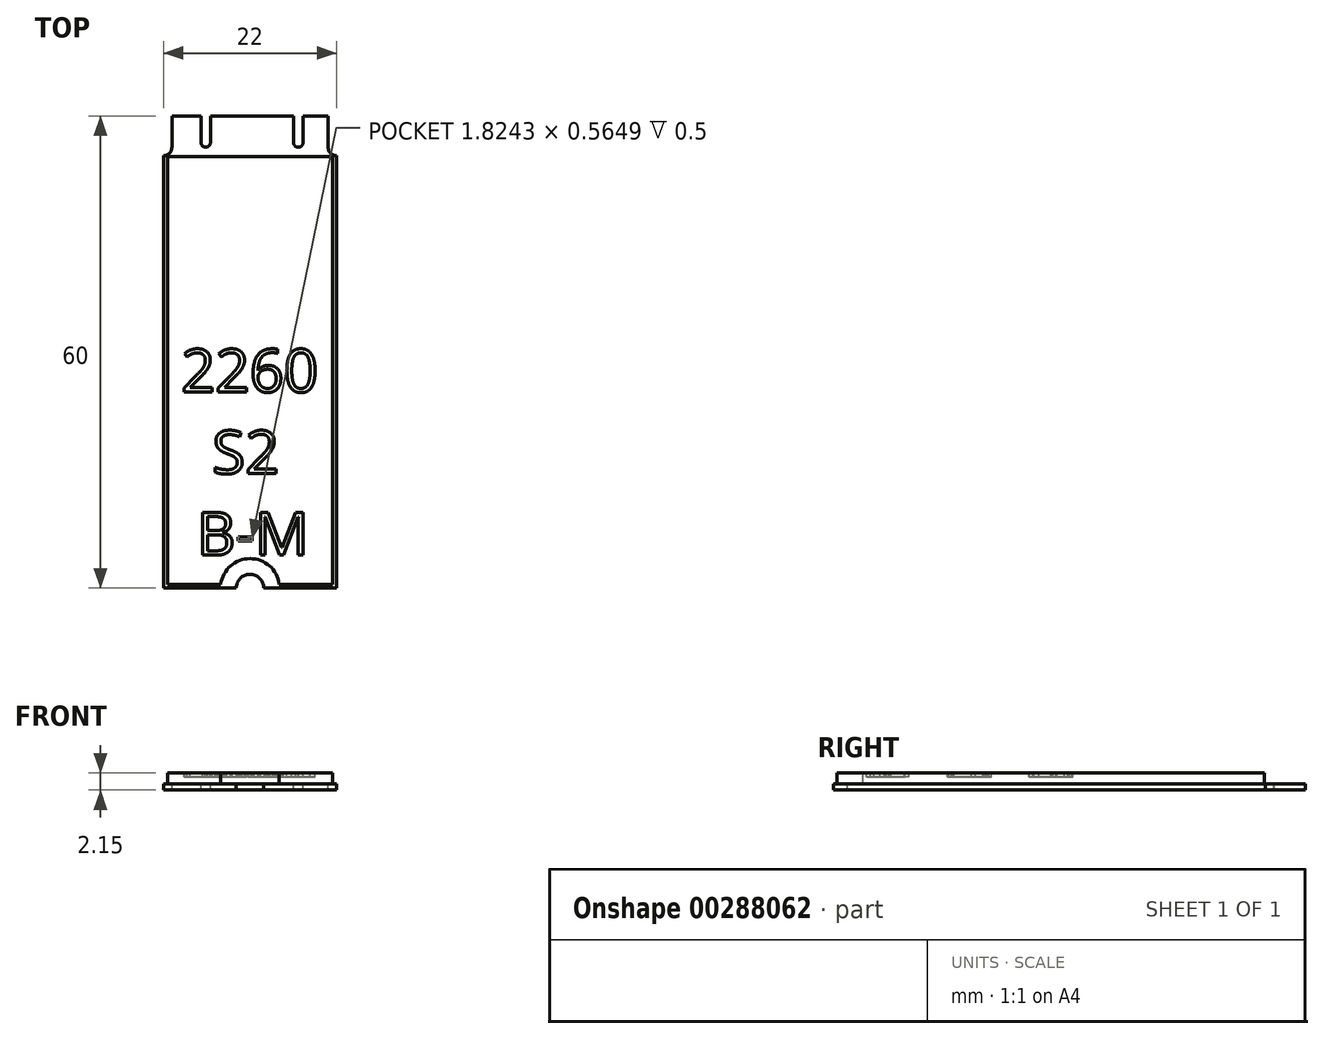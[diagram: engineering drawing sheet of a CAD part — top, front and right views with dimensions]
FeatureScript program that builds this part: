
annotation { "Feature Type Name" : "Feature", "Feature Type Description" : "" }
export const myFeature = defineFeature(function(context is Context, id is Id, definition is map)
    precondition{}
    {
        {
            assignVariable(context, id + "F0", {"name" : "thick", "anyValue" : .8});
        }
        {
            assignVariable(context, id + "F1", {"name" : "compheight", "anyValue" : 1.35});
        }
        {
            var Q0;
            Q0=qCreatedBy(makeId("Top.planeOp"),FACE);
            var sketch = newSketch(context, id + "F2", { "sketchPlane" : qUnion([Q0])});
            skLineSegment(sketch, "E0.bottom", {"start": v(-11, 30) * mm, "end": v(11, 30) * mm});
            skLineSegment(sketch, "E0.top", {"start": v(-11, -30) * mm, "end": v(11, -30) * mm});
            skLineSegment(sketch, "E0.left", {"start": v(-11, 30) * mm, "end": v(-11, -30) * mm});
            skLineSegment(sketch, "E0.right", {"start": v(11, 30) * mm, "end": v(11, -30) * mm});
            skPoint(sketch, "E0.middle", {"position": v(0, 0) * mm});
            skSolve(sketch);
        }
        {
            var Q0;
            Q0=qSketchRegion(id+"F2",true);
            extrude(context, id + "F3", {"entities" : qUnion([Q0]), "depth" : (getVariable(context, 'thick')) * mm});
        }
        {
            var Q0;
            Q0=makeQuery(id+"F3.opExtrude","CAP_FACE",FACE,{"disambiguationData":[OSD([sQuery(id+"F2.wireOp",EDGE,"E0.bottom"),sQuery(id+"F2.wireOp",EDGE,"E0.top"),sQuery(id+"F2.wireOp",EDGE,"E0.left"),sQuery(id+"F2.wireOp",EDGE,"E0.right")])],"isStart":false});
            var sketch = newSketch(context, id + "F4", { "sketchPlane" : qUnion([Q0])});
            skLineSegment(sketch, "E1.bottom", {"start": v(-10.5, -29.5) * mm, "end": v(10.5, -29.5) * mm});
            skLineSegment(sketch, "E1.top", {"start": v(-10.5, 24.8) * mm, "end": v(10.5, 24.8) * mm});
            skLineSegment(sketch, "E1.left", {"start": v(-10.5, -29.5) * mm, "end": v(-10.5, 24.8) * mm});
            skLineSegment(sketch, "E1.right", {"start": v(10.5, -29.5) * mm, "end": v(10.5, 24.8) * mm});
            skLineSegment(sketch, "E2", {"start": v(0, -30) * mm, "end": v(0, -29.5) * mm, "construction": true});
            skLineSegment(sketch, "E3", {"start": v(10.5, -2.35) * mm, "end": v(11, -2.35) * mm, "construction": true});
            skLineSegment(sketch, "E4", {"start": v(0, 24.8) * mm, "end": v(0, 30) * mm, "construction": true});
            skSolve(sketch);
        }
        {
            var Q0;
            Q0=qSketchRegion(id+"F4",true);
            extrude(context, id + "F5", {"entities" : qUnion([Q0]), "operationType" : NewBodyOperationType.ADD, "depth" : (getVariable(context, 'compheight')) * mm});
        }
        {
            var Q0;
            Q0=makeQuery(id+"F3.opExtrude","CAP_FACE",FACE,{"disambiguationData":[OSD([sQuery(id+"F2.wireOp",EDGE,"E0.bottom"),sQuery(id+"F2.wireOp",EDGE,"E0.top"),sQuery(id+"F2.wireOp",EDGE,"E0.left"),sQuery(id+"F2.wireOp",EDGE,"E0.right")])],"isStart":false});
            var sketch = newSketch(context, id + "F6", { "sketchPlane" : qUnion([Q0])});
            skLineSegment(sketch, "E5", {"start": v(0, 30) * mm, "end": v(0, 24.8) * mm, "construction": true});
            skLineSegment(sketch, "E6", {"start": v(-9.92, 30) * mm, "end": v(-9.92, 26) * mm});
            skArc(sketch, "E7", {"start": v(-11, 24.93) * mm, "mid": v(-10.24, 25.24) * mm, "end": v(-9.92, 26) * mm});
            skLineSegment(sketch, "E8", {"start": v(-9.92, 30) * mm, "end": v(-11, 30) * mm});
            skLineSegment(sketch, "E9", {"start": v(-11, 30) * mm, "end": v(-11, 24.93) * mm});
            skLineSegment(sketch, "E10.MirrorCS", {"start": v(9.93, 30) * mm, "end": v(9.93, 26) * mm});
            skLineSegment(sketch, "E11.MirrorCS", {"start": v(9.93, 30) * mm, "end": v(11, 30) * mm});
            skLineSegment(sketch, "E12.MirrorCS", {"start": v(11, 30) * mm, "end": v(11, 24.93) * mm});
            skArc(sketch, "E13.MirrorCS", {"start": v(11, 24.93) * mm, "mid": v(10.24, 25.24) * mm, "end": v(9.93, 26) * mm});
            skLineSegment(sketch, "E14", {"start": v(-9.92, 30) * mm, "end": v(9.93, 30) * mm, "construction": true});
            skLineSegment(sketch, "E15", {"start": v(0, 30) * mm, "end": v(6.13, 30) * mm, "construction": true});
            skLineSegment(sketch, "E16", {"start": v(6.13, 30) * mm, "end": v(6.13, 26.6) * mm, "construction": true});
            skLineSegment(sketch, "E17", {"start": v(0, 30) * mm, "end": v(-5.63, 30) * mm, "construction": true});
            skLineSegment(sketch, "E18", {"start": v(-9.92, 26) * mm, "end": v(6.13, 26) * mm, "construction": true});
            skArc(sketch, "E19", {"start": v(5.53, 26.6) * mm, "mid": v(6.13, 26) * mm, "end": v(6.73, 26.6) * mm});
            skLineSegment(sketch, "E20", {"start": v(6.13, 26.6) * mm, "end": v(5.53, 26.6) * mm, "construction": true});
            skLineSegment(sketch, "E21", {"start": v(6.73, 26.6) * mm, "end": v(6.73, 30) * mm});
            skLineSegment(sketch, "E22", {"start": v(6.73, 30) * mm, "end": v(5.53, 30) * mm});
            skLineSegment(sketch, "E23", {"start": v(5.53, 30) * mm, "end": v(5.53, 26.6) * mm});
            skLineSegment(sketch, "E24", {"start": v(-6.23, 30) * mm, "end": v(-6.23, 26.62) * mm});
            skLineSegment(sketch, "E25", {"start": v(-5.03, 30) * mm, "end": v(-5.03, 26.62) * mm});
            skArc(sketch, "E26", {"start": v(-6.23, 26.62) * mm, "mid": v(-5.63, 26.02) * mm, "end": v(-5.03, 26.62) * mm});
            skLineSegment(sketch, "E27", {"start": v(-6.23, 26.62) * mm, "end": v(-5.03, 26.62) * mm, "construction": true});
            skLineSegment(sketch, "E28", {"start": v(-5.63, 30) * mm, "end": v(-5.63, 26.62) * mm, "construction": true});
            skLineSegment(sketch, "E29", {"start": v(-6.23, 30) * mm, "end": v(-5.03, 30) * mm});
            skSolve(sketch);
        }
        {
            var Q0;
            Q0=qSketchRegion(id+"F6",true);
            extrude(context, id + "F7", {"entities" : qUnion([Q0]), "operationType" : NewBodyOperationType.REMOVE, "endBound" : BoundingType.THROUGH_ALL, "oppositeDirection" : true, "depth" : 25 * mm});
        }
        {
            var Q0;
            Q0=makeQuery(id+"F3.opExtrude","CAP_FACE",FACE,{"disambiguationData":[OSD([sQuery(id+"F2.wireOp",EDGE,"E0.bottom"),sQuery(id+"F2.wireOp",EDGE,"E0.top"),sQuery(id+"F2.wireOp",EDGE,"E0.left"),sQuery(id+"F2.wireOp",EDGE,"E0.right")])],"isStart":true});
            var sketch = newSketch(context, id + "F8", { "sketchPlane" : qUnion([Q0])});
            skCircle(sketch, "E30", {"center": v(0, 30) * mm, "radius": 1.75 * mm});
            skSolve(sketch);
        }
        {
            var Q0;
            Q0=qSketchRegion(id+"F8",true);
            extrude(context, id + "F9", {"entities" : qUnion([Q0]), "operationType" : NewBodyOperationType.REMOVE, "endBound" : BoundingType.THROUGH_ALL, "oppositeDirection" : true, "depth" : 25 * mm});
        }
        {
            var Q0;
            Q0=makeQuery(id+"F5.opExtrude","CAP_FACE",FACE,{"disambiguationData":[OSD([sQuery(id+"F4.wireOp",EDGE,"E1.bottom"),sQuery(id+"F4.wireOp",EDGE,"E1.top"),sQuery(id+"F4.wireOp",EDGE,"E1.left"),sQuery(id+"F4.wireOp",EDGE,"E1.right")])],"isStart":false});
            var sketch = newSketch(context, id + "F10", { "sketchPlane" : qUnion([Q0])});
            skArc(sketch, "E31.0", {"start": v(1.68, -29.5) * mm, "mid": v(0, -28.25) * mm, "end": v(-1.68, -29.5) * mm});
            skArc(sketch, "E32.0", {"start": v(3.72, -29.5) * mm, "mid": v(0, -26.25) * mm, "end": v(-3.72, -29.5) * mm});
            skLineSegment(sketch, "E33", {"start": v(-1.68, -29.5) * mm, "end": v(-3.72, -29.5) * mm});
            skLineSegment(sketch, "E34", {"start": v(1.68, -29.5) * mm, "end": v(3.72, -29.5) * mm});
            skSolve(sketch);
        }
        {
            var Q0;
            Q0=qSketchRegion(id+"F10",true);
            var Q1;
            Q1=makeQuery(id+"F3.opExtrude","CAP_FACE",FACE,{"disambiguationData":[OSD([sQuery(id+"F2.wireOp",EDGE,"E0.bottom"),sQuery(id+"F2.wireOp",EDGE,"E0.top"),sQuery(id+"F2.wireOp",EDGE,"E0.left"),sQuery(id+"F2.wireOp",EDGE,"E0.right")])],"isStart":false});
            extrude(context, id + "F11", {"entities" : qUnion([Q0]), "operationType" : NewBodyOperationType.REMOVE, "endBound" : BoundingType.UP_TO_SURFACE, "oppositeDirection" : true, "endBoundEntityFace" : qUnion([Q1]), "depth" : 25 * mm});
        }
        {
            var Q0;
            Q0=makeQuery(id+"F5.opExtrude","CAP_FACE",FACE,{"disambiguationData":[OSD([sQuery(id+"F4.wireOp",EDGE,"E1.bottom"),sQuery(id+"F4.wireOp",EDGE,"E1.top"),sQuery(id+"F4.wireOp",EDGE,"E1.left"),sQuery(id+"F4.wireOp",EDGE,"E1.right")])],"isStart":false});
            var sketch = newSketch(context, id + "F12", { "sketchPlane" : qUnion([Q0])});
            skLineSegment(sketch, "E35", {"start": v(10.5, -29.5) * mm, "end": v(-10.5, 24.8) * mm, "construction": true});
            skText(sketch, "E36", { "text": "2260\n  S2\n B-M", "fontName": "OpenSans-Regular.ttf"});
            skPoint(sketch, "E37", {"position": v(0, -2.35) * mm});
            const initialGuessF12  = {"E36": [-0.00876, -0.00509, 1, 0, 0.00548]};
            skSetInitialGuess(sketch, initialGuessF12);
            skSolve(sketch);
        }
        {
            var Q0;
            Q0=qSketchRegion(id+"F12",true);
            extrude(context, id + "F13", {"entities" : qUnion([Q0]), "operationType" : NewBodyOperationType.REMOVE, "oppositeDirection" : true, "depth" : .5 * mm});
        }
    });
